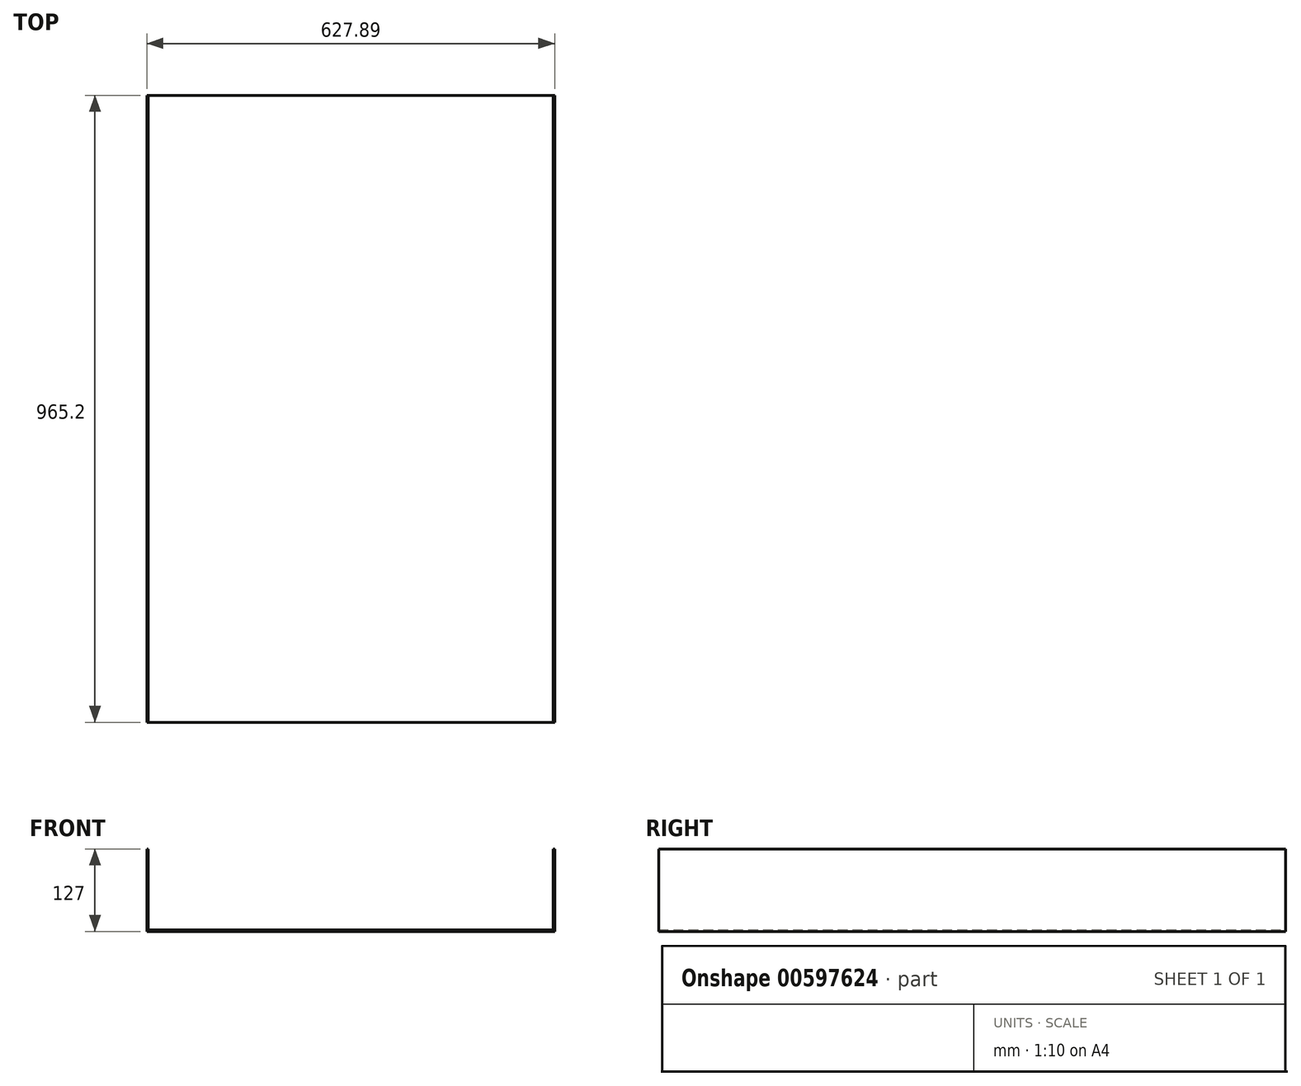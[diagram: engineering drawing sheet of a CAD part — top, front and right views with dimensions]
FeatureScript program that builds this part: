
annotation { "Feature Type Name" : "Feature", "Feature Type Description" : "" }
export const myFeature = defineFeature(function(context is Context, id is Id, definition is map)
    precondition{}
    {
        {
            var Q0;
            Q0=qCreatedBy(makeId("Front.planeOp"),FACE);
            var sketch = newSketch(context, id + "F0", { "sketchPlane" : qUnion([Q0])});
            skLineSegment(sketch, "E0", {"start": v(2.29, 127) * mm, "end": v(2.29, 2.29) * mm});
            skLineSegment(sketch, "E1", {"start": v(2.29, 2.29) * mm, "end": v(625.6, 2.29) * mm});
            skLineSegment(sketch, "E2", {"start": v(625.6, 2.29) * mm, "end": v(625.6, 127) * mm});
            skLineSegment(sketch, "E3.0", {"start": v(627.89, 0) * mm, "end": v(627.89, 127) * mm});
            skLineSegment(sketch, "E3.1", {"start": v(0, 0) * mm, "end": v(627.89, 0) * mm});
            skLineSegment(sketch, "E3.2", {"start": v(0, 127) * mm, "end": v(0, 0) * mm});
            skLineSegment(sketch, "E4", {"start": v(625.6, 127) * mm, "end": v(627.89, 127) * mm});
            skLineSegment(sketch, "E5", {"start": v(2.29, 127) * mm, "end": v(0, 127) * mm});
            skSolve(sketch);
        }
        {
            var Q0;
            Q0=makeQuery(id+"F0.imprint","IMPRINT",FACE,{"disambiguationData":[TD([[makeQuery(id+"F0.imprint","IMPRINT",EDGE,{"derivedFrom":sQuery(id+"F0.wireOp",EDGE,"E0")}),-1.0]])]});
            extrude(context, id + "F1", {"entities" : qUnion([Q0]), "depth" : 965.2 * mm, "offsetDistance" : 25.4 * mm});
        }
    });
